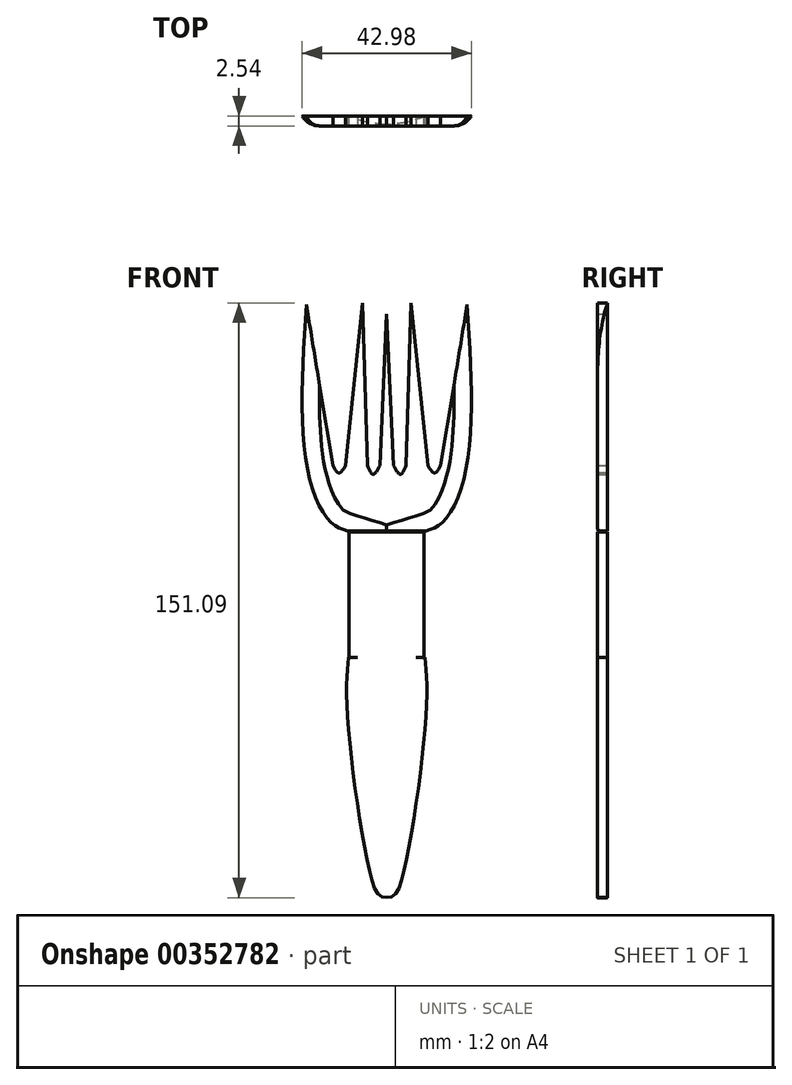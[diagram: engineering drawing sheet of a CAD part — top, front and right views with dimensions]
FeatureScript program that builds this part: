
annotation { "Feature Type Name" : "Feature", "Feature Type Description" : "" }
export const myFeature = defineFeature(function(context is Context, id is Id, definition is map)
    precondition{}
    {
        {
            var Q0;
            Q0=qCreatedBy(makeId("Front.planeOp"),FACE);
            var sketch = newSketch(context, id + "F0", { "sketchPlane" : qUnion([Q0])});
            skFitSpline(sketch, "E0", {"points": [v(0, -78.26) * mm, v(-4.56, -70.75) * mm, v(-10.04, -30.74) * mm, v(-9.7, -17.33) * mm], "startDerivative": vector(-32.48, -7.12) * mm, "endDerivative": vector(4.04, 31) * mm});
            skLineSegment(sketch, "E1", {"start": v(0, -78.26) * mm, "end": v(0, -17.08) * mm});
            skLineSegment(sketch, "E2", {"start": v(0, -17.08) * mm, "end": v(-9.7, -17.33) * mm});
            skFitSpline(sketch, "E3.MirrorCS", {"points": [v(0, -78.26) * mm, v(4.56, -70.75) * mm, v(10.04, -30.74) * mm, v(9.7, -17.33) * mm], "startDerivative": vector(32.48, -7.12) * mm, "endDerivative": vector(-4.04, 31) * mm});
            skLineSegment(sketch, "E4.MirrorCS", {"start": v(0, -17.08) * mm, "end": v(9.7, -17.33) * mm});
            skSolve(sketch);
        }
        {
            var Q0;
            Q0=makeQuery(id+"F0.imprint","IMPRINT",FACE,{"disambiguationData":[TD([[makeQuery(id+"F0.imprint","IMPRINT",EDGE,{"derivedFrom":sQuery(id+"F0.wireOp",EDGE,"E0")}),-1.0]])]});
            extrude(context, id + "F1", {"entities" : qUnion([Q0]), "endBound" : BoundingType.SYMMETRIC, "depth" : 2.54 * mm});
        }
        {
            var Q0;
            Q0=makeQuery(id+"F0.imprint","IMPRINT",FACE,{"disambiguationData":[TD([[makeQuery(id+"F0.imprint","IMPRINT",EDGE,{"derivedFrom":sQuery(id+"F0.wireOp",EDGE,"E1")}),-1.0]])]});
            extrude(context, id + "F2", {"entities" : qUnion([Q0]), "operationType" : NewBodyOperationType.ADD, "endBound" : BoundingType.SYMMETRIC, "depth" : 2.54 * mm});
        }
        {
            var Q0;
            Q0=qCreatedBy(makeId("Front.planeOp"),FACE);
            var sketch = newSketch(context, id + "F3", { "sketchPlane" : qUnion([Q0])});
            skLineSegment(sketch, "E5", {"start": v(-9.6, -17.27) * mm, "end": v(-9.6, 14.58) * mm});
            skLineSegment(sketch, "E6", {"start": v(-9.6, -17.27) * mm, "end": v(9.45, -17.27) * mm});
            skLineSegment(sketch, "E7", {"start": v(9.45, -17.27) * mm, "end": v(9.45, 14.58) * mm});
            skLineSegment(sketch, "E8", {"start": v(9.45, 14.58) * mm, "end": v(-9.6, 14.58) * mm});
            skSolve(sketch);
        }
        {
            var Q0;
            Q0=makeQuery(id+"F3.imprint","IMPRINT",FACE,{"disambiguationData":[TD([[makeQuery(id+"F3.imprint","IMPRINT",EDGE,{"derivedFrom":sQuery(id+"F3.wireOp",EDGE,"E5")}),-1.0]])]});
            extrude(context, id + "F4", {"entities" : qUnion([Q0]), "operationType" : NewBodyOperationType.ADD, "endBound" : BoundingType.SYMMETRIC, "depth" : 2.54 * mm});
        }
        {
            var Q0;
            Q0=qCreatedBy(makeId("Front.planeOp"),FACE);
            var sketch = newSketch(context, id + "F5", { "sketchPlane" : qUnion([Q0])});
            skLineSegment(sketch, "E9", {"start": v(0, 1.63) * mm, "end": v(0, 14.85) * mm});
            skLineSegment(sketch, "E10", {"start": v(0, 14.85) * mm, "end": v(-9.94, 14.85) * mm});
            skFitSpline(sketch, "E11", {"points": [v(-9.94, 14.85) * mm, v(-14.22, 17.05) * mm, v(-20.3, 31.43) * mm, v(-20.44, 72.39) * mm], "startDerivative": vector(-24.74, 7.57) * mm, "endDerivative": vector(5.49, 88.18) * mm});
            skFitSpline(sketch, "E12.MirrorCS", {"points": [v(9.94, 14.85) * mm, v(14.22, 17.05) * mm, v(20.3, 31.43) * mm, v(20.44, 72.39) * mm], "startDerivative": vector(24.74, 7.57) * mm, "endDerivative": vector(-5.49, 88.18) * mm});
            skLineSegment(sketch, "E13", {"start": v(-20.44, 72.39) * mm, "end": v(-13.7, 31.43) * mm});
            skFitSpline(sketch, "E14", {"points": [v(-13.7, 31.43) * mm, v(-12.14, 29.62) * mm, v(-10.46, 31.43) * mm], "startDerivative": vector(3.09, -5.46) * mm, "endDerivative": vector(3.4, 5.43) * mm});
            skLineSegment(sketch, "E15", {"start": v(-10.46, 31.43) * mm, "end": v(-6.18, 72.77) * mm});
            skLineSegment(sketch, "E16", {"start": v(-6.18, 72.77) * mm, "end": v(-4.88, 31.43) * mm});
            skFitSpline(sketch, "E17", {"points": [v(-4.88, 31.43) * mm, v(-3.46, 29.23) * mm, v(-1.77, 31.43) * mm], "startDerivative": vector(2.78, -6.64) * mm, "endDerivative": vector(3.43, 6.58) * mm});
            skLineSegment(sketch, "E18.MirrorCS", {"start": v(20.44, 72.39) * mm, "end": v(13.7, 31.43) * mm});
            skLineSegment(sketch, "E19.MirrorCS", {"start": v(10.46, 31.43) * mm, "end": v(6.18, 72.77) * mm});
            skLineSegment(sketch, "E20.MirrorCS", {"start": v(6.18, 72.77) * mm, "end": v(4.88, 31.43) * mm});
            skFitSpline(sketch, "E21.MirrorCS", {"points": [v(4.88, 31.43) * mm, v(3.46, 29.23) * mm, v(1.77, 31.43) * mm], "startDerivative": vector(-2.78, -6.64) * mm, "endDerivative": vector(-3.43, 6.58) * mm});
            skFitSpline(sketch, "E22.MirrorCS", {"points": [v(13.7, 31.43) * mm, v(12.14, 29.62) * mm, v(10.46, 31.43) * mm], "startDerivative": vector(-3.09, -5.46) * mm, "endDerivative": vector(-3.4, 5.43) * mm});
            skLineSegment(sketch, "E23", {"start": v(-1.77, 31.43) * mm, "end": v(0, 69.93) * mm});
            skLineSegment(sketch, "E24", {"start": v(0, 69.93) * mm, "end": v(1.77, 31.43) * mm});
            skLineSegment(sketch, "E25", {"start": v(0, 14.85) * mm, "end": v(9.94, 14.85) * mm});
            skSolve(sketch);
        }
        {
            var Q0;
            Q0=makeQuery(id+"F5.imprint","IMPRINT",FACE,{"disambiguationData":[TD([[makeQuery(id+"F5.imprint","IMPRINT",EDGE,{"derivedFrom":sQuery(id+"F5.wireOp",EDGE,"E10")}),-1.0]])]});
            extrude(context, id + "F6", {"entities" : qUnion([Q0]), "endBound" : BoundingType.SYMMETRIC, "depth" : 2.54 * mm});
        }
        {
            var Q0;
            Q0=makeQuery(id+"F6.opExtrude","CAP_EDGE",EDGE,{"disambiguationData":[OSD([sQuery(id+"F5.wireOp",EDGE,"E11")])],"isStart":false});
            fillet(context, id + "F7", {"entities" : qUnion([Q0]), "radius" : 5.08 * mm, "tangentPropagation" : true, "allowEdgeOverflow" : false});
        }
        {
            var Q0;
            Q0=makeQuery(id+"F6.opExtrude","CAP_EDGE",EDGE,{"disambiguationData":[OSD([sQuery(id+"F5.wireOp",EDGE,"E12.MirrorCS")])],"isStart":false});
            fillet(context, id + "F8", {"entities" : qUnion([Q0]), "radius" : 5.08 * mm, "tangentPropagation" : true, "allowEdgeOverflow" : false});
        }
    });
